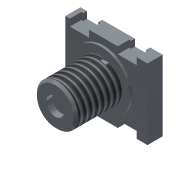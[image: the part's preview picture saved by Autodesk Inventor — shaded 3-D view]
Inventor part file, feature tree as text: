
AUTODESK INVENTOR PART (.ipt)
format: ipt  version: 2014 (Build 180170000, 170)  size: 227,840 bytes
history: native  units: in
note: dims shown in document units (in); Inventor stores cm internally (conversion verified against a paired STEP export)
features: sketch x9, extrude x8, reference x2, thread x1, chamfer x1, plane x1, revolve x1
ambient origin geometry x8: Origin, YZ Plane, XZ Plane, XY Plane, X Axis, Y Axis, Z Axis, Center Point
bodies: Solid1 (feature_tree)
feature tree (23):
  extrude  "Extrusion1"  Depth=0.464in
  extrude  "Extrusion2"  Depth=0.1in
  thread  "Thread1"  [1 undecoded]
  extrude  "Extrusion3"  Depth=0.315in
  chamfer  "Chamfer1"  Distance=0.315in
  plane  "Work Plane1"
  revolve  "Revolution1"  [1 undecoded]
  extrude  "Extrusion4"  Depth=0.015in TaperAngle=45.0deg
  extrude  "Extrusion5"  Depth=0.01in
  extrude  "Extrusion6"  TaperAngle=90.0deg  [1 undecoded]
  extrude  "Extrusion7"  Depth=0.04in TaperAngle=0.0deg
  extrude  "Extrusion8"  Depth=0.125in
  sketch  "Sketch1"  dims[d0=0.54in d1=0.464in]
  sketch  "Sketch2"  dims[d2=0.1in d3=0.0in d4=0.272in d5=0.29in]
  sketch  "Sketch3"  dims[d6=0.464in d7=0.232in d8=0.315in d9=0.0in]
  sketch  "Sketch4"  dims[d10=1.0in d11=0.0in d12=0.38in]
  sketch  "Sketch5"  dims[d13=0.015in d14=0.0in d15=0.015in d16=0.125in d17=45.0deg]
  sketch  "Sketch6"  dims[d18=0.29in d19=0.01in]
  reference  "Reference1"
  reference  "Reference2"
  sketch  "Sketch7"  dims[d20=0.025in d21=90.0deg]
  sketch  "Sketch8"  dims[d22=0.118in d23=0.04in d24=0.0in]
  sketch  "Sketch9"  dims[d25=0.125in d26=0.125in d27=0.125in d28=0.125in d29=0.54in d30=0.44in d32=0.045in d33=0.045in d34=0.19in d35=0.03in d36=0.075in d37=0.0in d38=0.125in d39=0.1in d40=0.0125in d41=0.075in d42=0.0in d43=0.1in d44=0.125in d45=0.0125in d46=0.075in d47=0.0in d48=0.1in d49=0.125in d50=0.0125in d51=0.0125in d52=0.075in d53=0.0in]
note: 3 required parameter values undecoded (feature->parameter linkage not recoverable at this tier; creation-order binding heuristic only, values carry confidence <= 0.55)